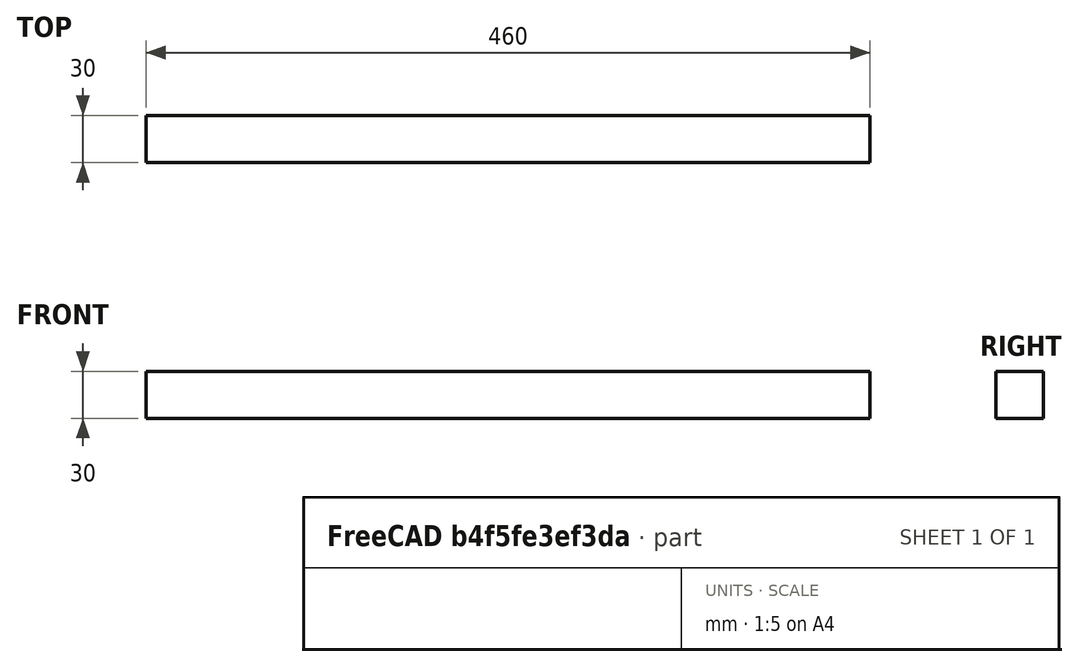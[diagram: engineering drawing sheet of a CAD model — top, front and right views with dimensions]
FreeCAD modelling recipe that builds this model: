
FCSTD DOCUMENT  (FreeCAD 0.20R29177 (Git))
Label: framesideright
License: All rights reserved
LicenseURL: http://en.wikipedia.org/wiki/All_rights_reserved
objects: Sketcher::SketchObject×1, PartDesign::Pad×1, PartDesign::Body×1
note: 4 computed .brp shape members not serialized (recipe doc carries the construction recipe); baked Part::Feature solids carry a one-line shape summary decoded from their .brp

FEATURE [Sketcher::SketchObject] Sketch
  FullyConstrained = true
  MapMode = 5
  Placement = pos=(0,0,0) rot=(0.57735,0.57735,0.57735;2.0944rad)
  Support = -> [YZ_Plane]
  sketch-geometry (4):
    g0: LineSegment StartX=0 StartY=0 StartZ=0 EndX=30 EndY=0 EndZ=0
    g1: LineSegment StartX=30 StartY=0 StartZ=0 EndX=30 EndY=30 EndZ=0
    g2: LineSegment StartX=30 StartY=30 StartZ=0 EndX=0 EndY=30 EndZ=0
    g3: LineSegment StartX=0 StartY=30 StartZ=0 EndX=0 EndY=0 EndZ=0
  constraints (11):
    c: Coincident(g0,g1)
    c: Coincident(g1,g2)
    c: Coincident(g2,g3)
    c: Coincident(g3,g0)
    c: Horizontal(g0)
    c: Horizontal(g2)
    c: Vertical(g1)
    c: Vertical(g3)
    c: Coincident(g0,g-1)
    c: Equal(g1,g2)
    c: DistanceX(g0,g0) = 30
FEATURE [PartDesign::Pad] Pad
  Direction = (1,1,1)
  Length = 460
  Length2 = 100
  Placement = pos=(0,0,0) rot=(0.57735,0.57735,0.57735;2.0944rad)
  Profile = -> Sketch
  Type = 0
FEATURE [PartDesign::Body] Body  label="framesideright"
  Group = -> [Sketch,Pad]
  Origin = -> Origin
  Tip = -> Pad
